FCSTD DOCUMENT  (FreeCAD 1.0R39109 (Git))
Label: StepperMotor_8mm_i500212644
License: All rights reserved
LicenseURL: https://en.wikipedia.org/wiki/All_rights_reserved
objects: Sketcher::SketchObject×2
note: 4 computed .brp shape members not serialized (recipe doc carries the construction recipe); baked Part::Feature solids carry a one-line shape summary decoded from their .brp

FEATURE [Sketcher::SketchObject] Sketch003  label="MasterSketch_TOP"
  ArcFitTolerance = 1e-06
  FullyConstrained = true
  MakeInternals = false
  MapMode = 5
  sketch-geometry (18):
    g0: LineSegment StartX=-4.65 StartY=-4 StartZ=0 EndX=4.65 EndY=-4 EndZ=0
    g1: LineSegment StartX=4.65 StartY=-4 StartZ=0 EndX=4.65 EndY=4 EndZ=0
    g2: LineSegment StartX=4.65 StartY=4 StartZ=0 EndX=-4.65 EndY=4 EndZ=0
    g3: LineSegment StartX=-4.65 StartY=4 StartZ=0 EndX=-4.65 EndY=-4 EndZ=0
    g4: GeomPoint [constr] X=0 Y=0 Z=0
    g5: LineSegment [constr] StartX=4.65 StartY=2e-16 StartZ=0 EndX=-4.65 EndY=2e-16 EndZ=0
    g6: LineSegment StartX=-4.65 StartY=2 StartZ=0 EndX=-5.05 EndY=2 EndZ=0
    g7: LineSegment StartX=-5.05 StartY=2 StartZ=0 EndX=-5.05 EndY=-2 EndZ=0
    g8: LineSegment StartX=-5.05 StartY=-2 StartZ=0 EndX=-4.65 EndY=-2 EndZ=0
    g9: LineSegment StartX=-4.65 StartY=-2 StartZ=0 EndX=-4.65 EndY=2 EndZ=0
    g10: LineSegment StartX=-5.05 StartY=0.4 StartZ=0 EndX=-8.55 EndY=0.4 EndZ=0
    g11: LineSegment StartX=-8.55 StartY=0.4 StartZ=0 EndX=-8.55 EndY=-0.4 EndZ=0
    g12: LineSegment StartX=-8.55 StartY=-0.4 StartZ=0 EndX=-5.05 EndY=-0.4 EndZ=0
    g13: LineSegment StartX=-5.05 StartY=-0.4 StartZ=0 EndX=-5.05 EndY=0.4 EndZ=0
    g14: LineSegment StartX=-8.55 StartY=1.15 StartZ=0 EndX=-8.55 EndY=-1.15 EndZ=0
    g15: LineSegment StartX=-6.05 StartY=-1.15 StartZ=0 EndX=-6.05 EndY=1.15 EndZ=0
    g16: LineSegment StartX=-6.05 StartY=1.15 StartZ=0 EndX=-8.55 EndY=1.15 EndZ=0
    g17: LineSegment StartX=-8.55 StartY=-1.15 StartZ=0 EndX=-6.05 EndY=-1.15 EndZ=0
  constraints (46):
    c: Coincident(g0,g1)
    c: Coincident(g1,g2)
    c: Coincident(g2,g3)
    c: Coincident(g3,g0)
    c: Horizontal(g0)
    c: Horizontal(g2)
    c: Vertical(g1)
    c: Vertical(g3)
    c: Symmetric(g2,g0,g4)
    c: Distance(g1,g3) = 9.3
    c: Distance(g0,g2) = 8
    c: Coincident(g4,g-1)
    c: Symmetric(g1,g1,g5)
    c: Symmetric(g3,g3,g5)
    c: Coincident(g6,g7)
    c: Coincident(g7,g8)
    c: Coincident(g8,g9)
    c: Coincident(g9,g6)
    c: Horizontal(g6)
    c: Horizontal(g8)
    c: Distance(g7,g9) = 0.4
    c: Tangent(g9,g3)
    c: Symmetric(g7,g6,g5)
    c: Distance(g8,g6) = 4
    c: Coincident(g10,g11)
    c: Coincident(g11,g12)
    c: Coincident(g12,g13)
    c: Coincident(g13,g10)
    c: Horizontal(g10)
    c: Horizontal(g12)
    c: Vertical(g13)
    c: Distance(g11,g13) = 3.5
    c: Distance(g10,g12) = 0.8
    c: PointOnObject(g10,g7)
    c: Coincident(g15,g16)
    c: Coincident(g16,g14)
    c: Vertical(g15)
    c: Horizontal(g16)
    c: Distance(g14,g15) = 2.5
    c: Distance(g14,g16) = 2.3
    c: Coincident(g17,g14)
    c: Coincident(g17,g15)
    c: Horizontal(g17)
    c: Symmetric(g14,g14,g5)
    c: Symmetric(g11,g10,g5)
    c: Tangent(g11,g14) = -1.5708
FEATURE [Sketcher::SketchObject] Sketch  label="MasterSketch_SIDE"
  ArcFitTolerance = 1e-06
  ExternalGeometry = -> [Sketch003]
  FullyConstrained = true
  MakeInternals = false
  MapMode = 5
  Placement = pos=(0,0,0) rot=(0.57735,0.57735,0.57735;2.0944rad)
  sketch-geometry (1):
    g0: Circle CenterX=0 CenterY=0 CenterZ=0 NormalX=0 NormalY=0 NormalZ=1 AngleXU=0 Radius=4
  constraints (2):
    c: Coincident(g0,g-1)
    c: PointOnObject(g-3,g0)
